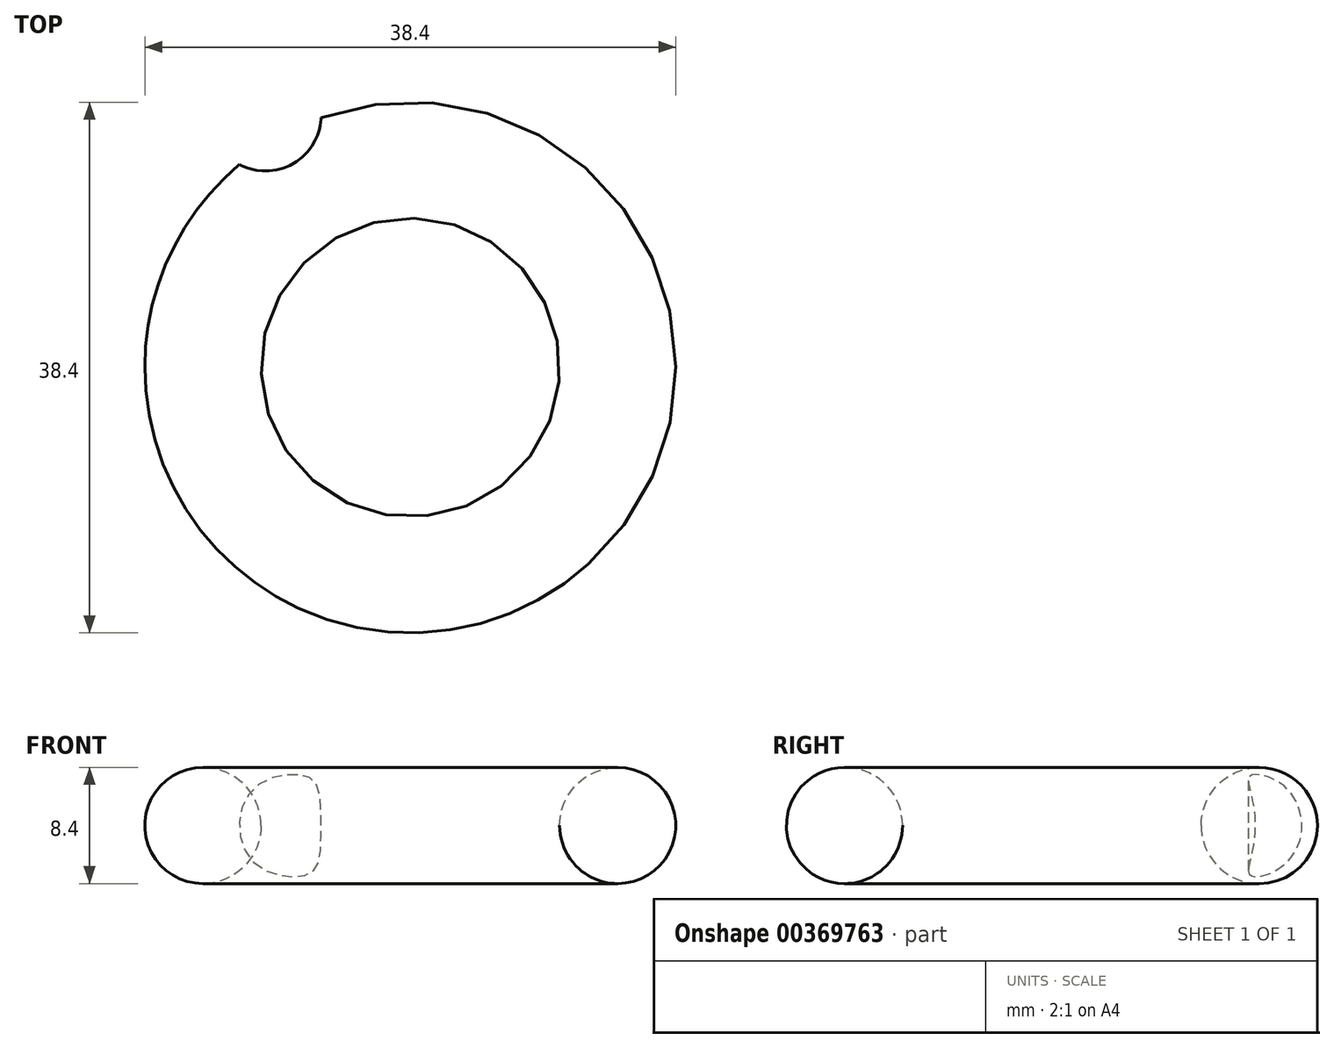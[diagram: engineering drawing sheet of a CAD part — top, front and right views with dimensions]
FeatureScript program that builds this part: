
annotation { "Feature Type Name" : "Feature", "Feature Type Description" : "" }
export const myFeature = defineFeature(function(context is Context, id is Id, definition is map)
    precondition{}
    {
        {
            var Q0;
            Q0=qCreatedBy(makeId("Front.planeOp"),FACE);
            var sketch = newSketch(context, id + "F0", { "sketchPlane" : qUnion([Q0])});
            skArc(sketch, "E0", {"start": v(-12, 9) * mm, "mid": v(-6.32, 6.03) * mm, "end": v(0, 5) * mm});
            skArc(sketch, "E1", {"start": v(-12, 9) * mm, "mid": v(-19.74, 6.58) * mm, "end": v(-15, 0) * mm});
            skLineSegment(sketch, "E2", {"start": v(0, 5) * mm, "end": v(0, 0) * mm});
            skLineSegment(sketch, "E3", {"start": v(0, 0) * mm, "end": v(-15, 0) * mm});
            skSolve(sketch);
        }
        {
            var Q0;
            Q0=sQuery(id+"F0.wireOp",EDGE,"E0");
            var Q1;
            Q1=sQuery(id+"F0.wireOp",EDGE,"E1");
            var Q2;
            Q2=sQuery(id+"F0.wireOp",EDGE,"E3");
            var Q3;
            Q3=sQuery(id+"F0.wireOp",EDGE,"E2");
            revolve(context, id + "F1", {"bodyType" : ToolBodyType.SURFACE, "surfaceEntities" : qUnion([Q0, Q1, Q2]), "axis" : qUnion([Q3]), "revolveType" : RevolveType.FULL});
        }
        {
            var Q0;
            Q0=qCreatedBy(makeId("Front.planeOp"),FACE);
            var sketch = newSketch(context, id + "F2", { "sketchPlane" : qUnion([Q0])});
            skCircle(sketch, "E4", {"center": v(-15, 5) * mm, "radius": 4.2 * mm});
            skSolve(sketch);
        }
        {
            var Q0;
            Q0 = qSketchRegion(id + "F2", true);
            var Q1;
            Q1=sQuery(id+"F0.wireOp",EDGE,"E2");
            revolve(context, id + "F3", {"entities" : qUnion([Q0]), "axis" : qUnion([Q1]), "revolveType" : RevolveType.FULL});
        }
        {
            var Q0;
            Q0=qCreatedBy(makeId("Top.planeOp"),FACE);
            var sketch = newSketch(context, id + "F4", { "sketchPlane" : qUnion([Q0])});
            skCircle(sketch, "E5", {"center": v(-10.46, 18.21) * mm, "radius": 4 * mm});
            skSolve(sketch);
        }
        {
            var Q0;
            Q0=makeQuery(id+"F4.imprint","IMPRINT",FACE,{"disambiguationData":[TD([[makeQuery(id+"F4.imprint","IMPRINT",EDGE,{"derivedFrom":sQuery(id+"F4.wireOp",EDGE,"E5")}),1.0]])]});
            extrude(context, id + "F5", {"entities" : qUnion([Q0]), "operationType" : NewBodyOperationType.REMOVE, "depth" : 25 * mm});
        }
        {
            var Q0;
            Q0 = qSketchRegion(id + "F4", true);
            extrude(context, id + "F6", {"entities" : qUnion([Q0]), "operationType" : NewBodyOperationType.REMOVE, "depth" : 25 * mm});
        }
    });
